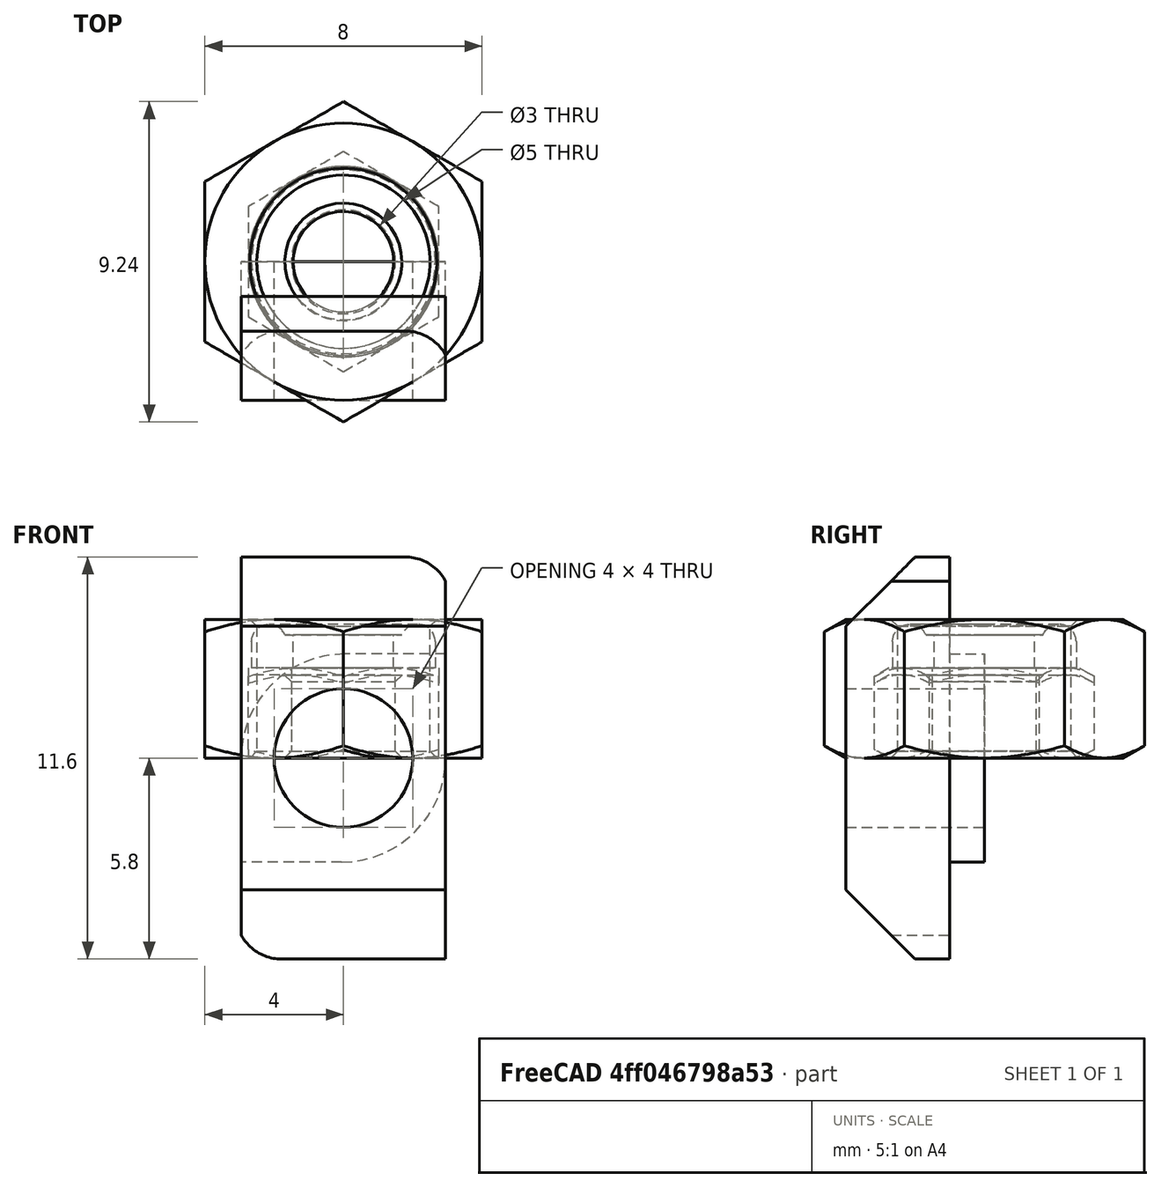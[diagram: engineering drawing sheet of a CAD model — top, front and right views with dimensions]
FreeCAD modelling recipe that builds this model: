
FCSTD DOCUMENT  (FreeCAD 0.14R3692 (Git))
Label: nuts
License: CC-BY 3.0
LicenseURL: http://creativecommons.org/licenses/by/3.0/
objects: Part::Feature×5, Part::Mirroring×1, Part::MultiFuse×1
note: 7 computed .brp shape members not serialized (recipe doc carries the construction recipe); baked Part::Feature solids carry a one-line shape summary decoded from their .brp

FEATURE [Part::Feature] Part__Feature  label="nut-m5"
  shape: bbox 9.238 x 9.238 x 4 mm, 23 faces (baked)
FEATURE [Part::Feature] Part__Feature001  label="hammer-nut-6mm-m4-orig"
  shape: bbox 5.9 x 4 x 11.6 mm, 18 faces (baked)
FEATURE [Part::Mirroring] Part__Mirroring  label="hammer-nut-6mm-m4"
  Base = (0,0,0)
  Normal = (1,0,0)
  Source = -> Part__Feature001
FEATURE [Part::Feature] Part__Feature002  label="nut-m3"
  shape: bbox 6.35 x 6.35 x 2.4 mm, 29 faces (baked)
FEATURE [Part::Feature] Part__Feature003  label="Nyloc-nut-M3"
  shape: bbox 6.35 x 6.35 x 3.86 mm, 32 faces (baked)
FEATURE [Part::Feature] Part__Feature004  label="Nyloc-nut-M3-nyloc"
  shape: bbox 3.5 x 3.5 x 0.95 mm, 4 faces (baked)
FEATURE [Part::MultiFuse] Fusion  label="nyloc-nut-m3"
  Shapes = -> [Part__Feature003,Part__Feature004]
